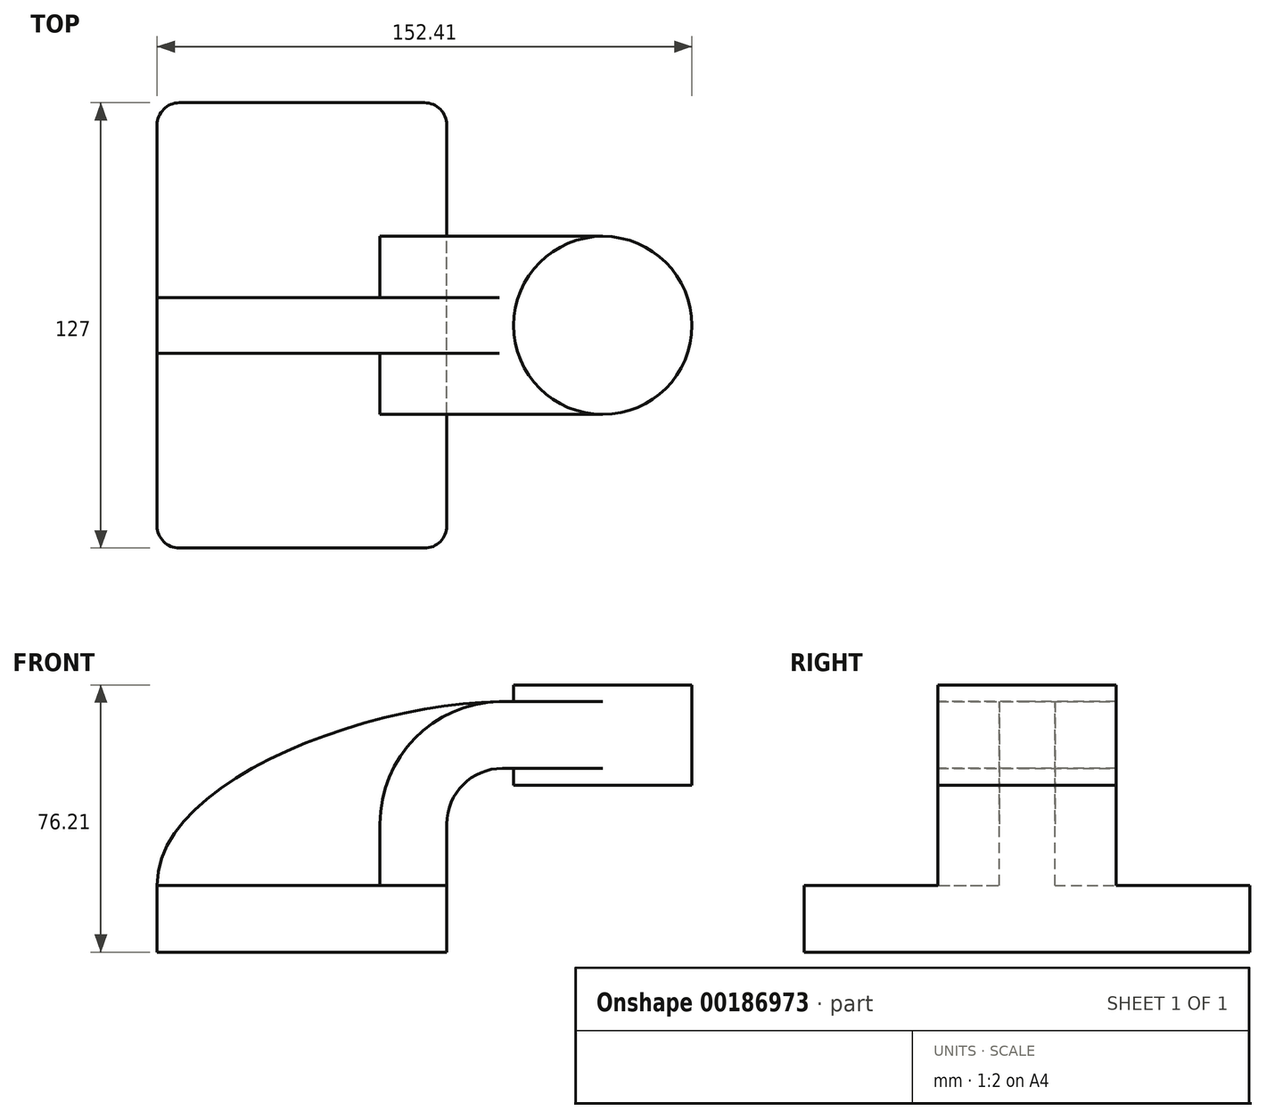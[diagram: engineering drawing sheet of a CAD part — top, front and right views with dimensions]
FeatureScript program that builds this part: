
annotation { "Feature Type Name" : "Feature", "Feature Type Description" : "" }
export const myFeature = defineFeature(function(context is Context, id is Id, definition is map)
    precondition{}
    {
        {
            var Q0;
            Q0=qCreatedBy(makeId("Front.planeOp"),FACE);
            var sketch = newSketch(context, id + "F0", { "sketchPlane" : qUnion([Q0])});
            skLineSegment(sketch, "E0.bottom", {"start": v(41.28, -9.52) * mm, "end": v(-41.28, -9.53) * mm});
            skLineSegment(sketch, "E0.top", {"start": v(41.28, 9.53) * mm, "end": v(-41.28, 9.53) * mm});
            skLineSegment(sketch, "E0.left", {"start": v(41.28, -9.52) * mm, "end": v(41.28, 9.53) * mm});
            skLineSegment(sketch, "E0.right", {"start": v(-41.28, -9.52) * mm, "end": v(-41.28, 9.53) * mm});
            skPoint(sketch, "E0.middle", {"position": v(0, 0) * mm});
            skLineSegment(sketch, "E1.bottom", {"start": v(60.32, 38.1) * mm, "end": v(111.12, 38.1) * mm});
            skLineSegment(sketch, "E1.top", {"start": v(60.32, 66.68) * mm, "end": v(111.12, 66.68) * mm});
            skLineSegment(sketch, "E1.left", {"start": v(60.32, 38.1) * mm, "end": v(60.32, 66.68) * mm});
            skLineSegment(sketch, "E1.right", {"start": v(111.12, 38.1) * mm, "end": v(111.12, 66.68) * mm});
            skPoint(sketch, "E1.middle", {"position": v(85.72, 52.39) * mm});
            skLineSegment(sketch, "E2", {"start": v(41.28, 9.53) * mm, "end": v(41.28, 27) * mm});
            skArc(sketch, "E3", {"start": v(41.27, 27) * mm, "mid": v(45.92, 38.23) * mm, "end": v(57.15, 42.88) * mm});
            skLineSegment(sketch, "E4", {"start": v(57.15, 42.88) * mm, "end": v(85.72, 42.88) * mm});
            skLineSegment(sketch, "E5.0", {"start": v(57.15, 61.93) * mm, "end": v(85.72, 61.93) * mm});
            skArc(sketch, "E5.1", {"start": v(22.23, 27) * mm, "mid": v(32.45, 51.7) * mm, "end": v(57.15, 61.93) * mm});
            skLineSegment(sketch, "E5.2", {"start": v(22.23, 9.53) * mm, "end": v(22.23, 27) * mm});
            skLineSegment(sketch, "E6", {"start": v(85.72, 38.1) * mm, "end": v(85.72, 66.68) * mm});
            skFitSpline(sketch, "E7", {"points": [v(-41.28, 9.53) * mm, v(57.15, 61.93) * mm], "startDerivative": vector(-0.55, 90.07) * mm, "endDerivative": vector(114.11, 0.97) * mm});
            skSolve(sketch);
        }
        {
            var Q0;
            Q0=makeQuery(id+"F0.imprint","IMPRINT",FACE,{"disambiguationData":[TD([[makeQuery(id+"F0.imprint","IMPRINT",EDGE,{"derivedFrom":sQuery(id+"F0.wireOp",EDGE,"E0.bottom")}),-1.0]])]});
            extrude(context, id + "F1", {"entities" : qUnion([Q0]), "endBound" : BoundingType.SYMMETRIC, "depth" : 127 * mm});
        }
        {
            var Q0;
            {var subQ1=sQuery(id+"F0.wireOp",EDGE,"E2");Q0=makeQuery(id+"F0.imprint","IMPRINT",FACE,{"disambiguationData":[TD([[makeQuery(id+"F0.imprint","IMPRINT",EDGE,{"derivedFrom":subQ1}),1.0]])]});}
            extrude(context, id + "F2", {"entities" : qUnion([Q0]), "operationType" : NewBodyOperationType.ADD, "endBound" : BoundingType.SYMMETRIC, "depth" : 50.8 * mm});
        }
        {
            var Q0;
            {var subQ3=sQuery(id+"F0.wireOp",EDGE,"E5.2");Q0=makeQuery(id+"F0.imprint","IMPRINT",FACE,{"disambiguationData":[TD([[makeQuery(id+"F0.imprint","IMPRINT",EDGE,{"derivedFrom":subQ3}),1.0]])]});}
            extrude(context, id + "F3", {"entities" : qUnion([Q0]), "operationType" : NewBodyOperationType.ADD, "endBound" : BoundingType.SYMMETRIC, "depth" : 15.88 * mm});
        }
        {
            var Q0;
            Q0=makeQuery(id+"F2.opExtrude","SWEPT_FACE",FACE,{"disambiguationData":[OSD([sQuery(id+"F0.wireOp",EDGE,"E1.left")])]});
            var Q1;
            Q1=sQuery(id+"F0.wireOp",VERTEX,"E1.middle");
            extrude(context, id + "F4", {"entities" : qUnion([Q0]), "operationType" : NewBodyOperationType.ADD, "endBound" : BoundingType.UP_TO_VERTEX, "endBoundEntityVertex" : qUnion([Q1]), "depth" : 25.4 * mm});
        }
        {
            var Q0;
            {var subQ0=sQuery(id+"F0.wireOp",EDGE,"E1.right");Q0=makeQuery(id+"F0.imprint","IMPRINT",FACE,{"disambiguationData":[TD([[makeQuery(id+"F0.imprint","IMPRINT",EDGE,{"derivedFrom":subQ0}),1.0]])]});}
            var Q1;
            Q1=sQuery(id+"F0.wireOp",EDGE,"E6");
            revolve(context, id + "F5", {"operationType" : NewBodyOperationType.ADD, "entities" : qUnion([Q0]), "axis" : qUnion([Q1]), "revolveType" : RevolveType.FULL});
        }
        {
            var Q0;
            Q0=makeQuery(id+"F1.opExtrude","CAP_EDGE",EDGE,{"disambiguationData":[OSD([sQuery(id+"F0.wireOp",EDGE,"E0.left")])],"isStart":true});
            var Q1;
            Q1=makeQuery(id+"F1.opExtrude","CAP_EDGE",EDGE,{"disambiguationData":[OSD([sQuery(id+"F0.wireOp",EDGE,"E0.right")])],"isStart":true});
            var Q2;
            Q2=makeQuery(id+"F1.opExtrude","CAP_EDGE",EDGE,{"disambiguationData":[OSD([sQuery(id+"F0.wireOp",EDGE,"E0.right")])],"isStart":false});
            var Q3;
            Q3=makeQuery(id+"F1.opExtrude","CAP_EDGE",EDGE,{"disambiguationData":[OSD([sQuery(id+"F0.wireOp",EDGE,"E0.left")])],"isStart":false});
            fillet(context, id + "F6", {"entities" : qUnion([Q0, Q1, Q2, Q3]), "radius" : 6.35 * mm, "tangentPropagation" : true, "allowEdgeOverflow" : false});
        }
    });
